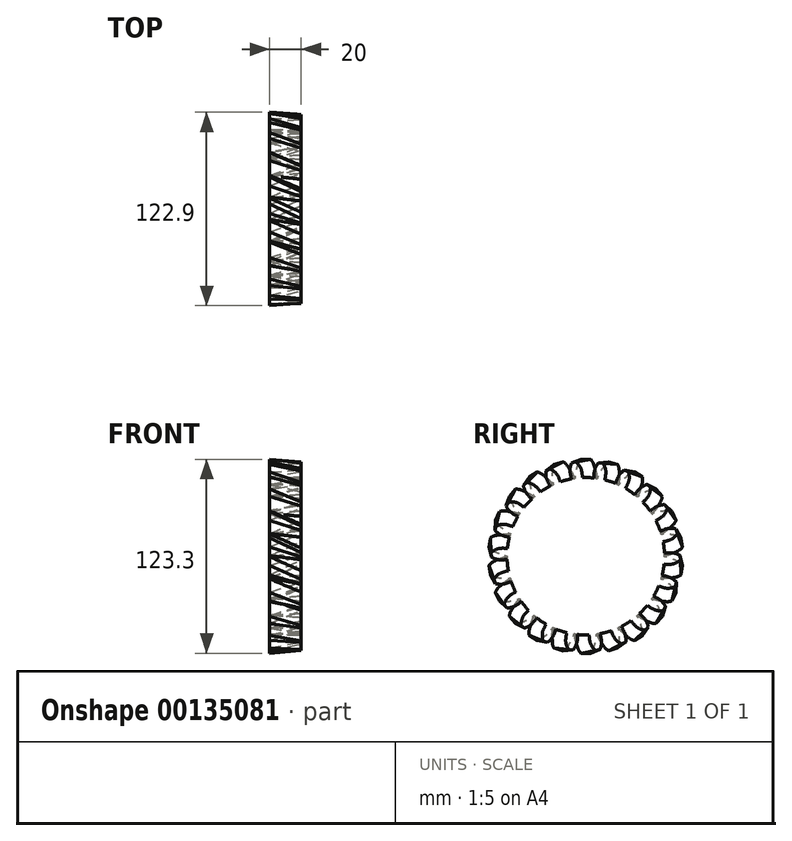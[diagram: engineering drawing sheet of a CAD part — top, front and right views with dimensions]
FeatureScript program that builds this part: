
annotation { "Feature Type Name" : "Feature", "Feature Type Description" : "" }
export const myFeature = defineFeature(function(context is Context, id is Id, definition is map)
    precondition{}
    {
        {
            var Q0;
            Q0=qCreatedBy(makeId("Right.planeOp"),FACE);
            var sketch = newSketch(context, id + "F0", { "sketchPlane" : qUnion([Q0])});
            skCircle(sketch, "E0", {"center": v(0, 0) * mm, "radius": 50 * mm});
            skSolve(sketch);
        }
        {
            var Q0;
            Q0=makeQuery(id+"F0.imprint","IMPRINT",FACE,{"disambiguationData":[TD([[makeQuery(id+"F0.imprint","IMPRINT",EDGE,{"derivedFrom":sQuery(id+"F0.wireOp",EDGE,"E0")}),1.0]])]});
            extrude(context, id + "F1", {"entities" : qUnion([Q0]), "depth" : 20 * mm});
        }
        {
            var Q0;
            Q0=qCreatedBy(makeId("Right.planeOp"),FACE);
            var sketch = newSketch(context, id + "F2", { "sketchPlane" : qUnion([Q0])});
            skArc(sketch, "E1.0.0", {"start": v(6.83, 49.53) * mm, "mid": v(0, 50) * mm, "end": v(-6.83, 49.53) * mm});
            skLineSegment(sketch, "E2", {"start": v(-3, 61.65) * mm, "end": v(3, 61.65) * mm});
            skFitSpline(sketch, "E3", {"points": [v(-3, 61.65) * mm, v(-5.61, 56.54) * mm, v(-6.83, 49.53) * mm], "startDerivative": vector(-10.67, -10.92) * mm, "endDerivative": vector(2.14, -14.63) * mm});
            skFitSpline(sketch, "E4.MirrorCS", {"points": [v(3, 61.65) * mm, v(5.61, 56.54) * mm, v(6.83, 49.53) * mm], "startDerivative": vector(10.67, -10.92) * mm, "endDerivative": vector(-2.14, -14.63) * mm});
            skSolve(sketch);
        }
        {
            var Q0;
            Q0=makeQuery(id+"F1.opExtrude","CAP_FACE",FACE,{"disambiguationData":[OSD([sQuery(id+"F0.wireOp",EDGE,"E0")])],"isStart":false});
            var sketch = newSketch(context, id + "F3", { "sketchPlane" : qUnion([Q0])});
            skFitSpline(sketch, "E5", {"points": [v(-9.1, 49.16) * mm, v(-10.02, 54.83) * mm, v(-9.07, 59.26) * mm], "startDerivative": vector(-2.74, 11.06) * mm, "endDerivative": vector(2.91, 9.12) * mm});
            skLineSegment(sketch, "E6", {"start": v(-9.07, 59.26) * mm, "end": v(-6.14, 59.8) * mm});
            skFitSpline(sketch, "E7", {"points": [v(-6.14, 59.8) * mm, v(-3.2, 55.98) * mm, v(-2.12, 49.95) * mm], "startDerivative": vector(7.24, -7.36) * mm, "endDerivative": vector(0.93, -12.32) * mm});
            skArc(sketch, "E8.0", {"start": v(-2.12, 49.95) * mm, "mid": v(-5.63, 49.68) * mm, "end": v(-9.1, 49.16) * mm});
            skSolve(sketch);
        }
        {
            var Q1;
            Q1=makeQuery(id+"F2.imprint","IMPRINT",FACE,{"disambiguationData":[TD([[makeQuery(id+"F2.imprint","IMPRINT",EDGE,{"derivedFrom":sQuery(id+"F2.wireOp",EDGE,"E1.0.0")}),-1.0]])]});
            var Q2;
            Q2=makeQuery(id+"F3.imprint","IMPRINT",FACE,{"disambiguationData":[TD([[makeQuery(id+"F3.imprint","IMPRINT",EDGE,{"derivedFrom":sQuery(id+"F3.wireOp",EDGE,"E5")}),-1.0]])]});
            loft(context, id + "F4", {"sheetProfilesArray" : [{ "sheetProfileEntities" : qUnion([Q1]) }, { "sheetProfileEntities" : qUnion([Q2]) }]});
        }
        {
            var Q0;
            Q0=qCreatedBy(makeId("Front.planeOp"),FACE);
            var sketch = newSketch(context, id + "F5", { "sketchPlane" : qUnion([Q0])});
            skLineSegment(sketch, "E9", {"start": v(62.03, 0) * mm, "end": v(-44.15, 0) * mm});
            skSolve(sketch);
        }
        {
            var Q0;
            Q0=makeQuery(id+"F4.opLoft","SWEPT_BODY",BODY,{"disambiguationData":[OSD([makeQuery(id+"F2.imprint","IMPRINT",FACE,{"disambiguationData":[TD([[makeQuery(id+"F2.imprint","IMPRINT",EDGE,{"derivedFrom":sQuery(id+"F2.wireOp",EDGE,"E1.0.0")}),-1.0]])]}),makeQuery(id+"F3.imprint","IMPRINT",FACE,{"disambiguationData":[TD([[makeQuery(id+"F3.imprint","IMPRINT",EDGE,{"derivedFrom":sQuery(id+"F3.wireOp",EDGE,"E5")}),-1.0]])]})])]});
            var Q1;
            Q1=sQuery(id+"F5.wireOp",EDGE,"E9");
            circularPattern(context, id + "F6", {"operationType" : NewBodyOperationType.ADD, "entities" : qUnion([Q0]), "axis" : qUnion([Q1]), "angle" : 360 * degree, "instanceCount" : 22, "equalSpace" : true});
        }
    });
